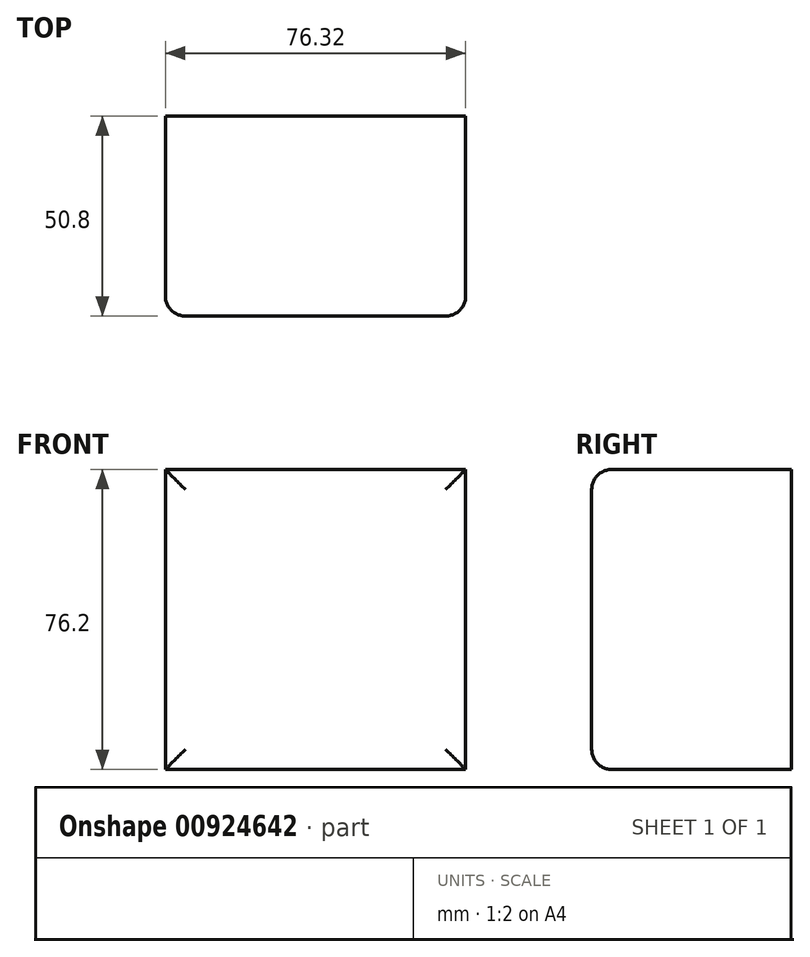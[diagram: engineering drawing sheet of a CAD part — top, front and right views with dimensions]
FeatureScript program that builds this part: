
annotation { "Feature Type Name" : "Feature", "Feature Type Description" : "" }
export const myFeature = defineFeature(function(context is Context, id is Id, definition is map)
    precondition{}
    {
        {
            var Q0;
            Q0=qCreatedBy(makeId("Front.planeOp"),FACE);
            var sketch = newSketch(context, id + "F0", { "sketchPlane" : qUnion([Q0])});
            skLineSegment(sketch, "E0", {"start": v(0, 0) * mm, "end": v(76.32, 0) * mm});
            skLineSegment(sketch, "E1", {"start": v(76.32, 0) * mm, "end": v(76.32, 76.2) * mm});
            skLineSegment(sketch, "E2", {"start": v(76.32, 76.2) * mm, "end": v(0, 76.2) * mm});
            skLineSegment(sketch, "E3", {"start": v(0, 76.2) * mm, "end": v(0, 0) * mm});
            skSolve(sketch);
        }
        {
            var Q0;
            Q0=makeQuery(id+"F0.imprint","IMPRINT",FACE,{"disambiguationData":[TD([[makeQuery(id+"F0.imprint","IMPRINT",EDGE,{"derivedFrom":sQuery(id+"F0.wireOp",EDGE,"E0")}),1.0]])]});
            extrude(context, id + "F1", {"entities" : qUnion([Q0]), "endBound" : BoundingType.SYMMETRIC, "depth" : 50.8 * mm, "offsetDistance" : 25.4 * mm, "hasSecondDirection" : true, "secondDirectionOppositeDirection" : true, "secondDirectionDepth" : 25.4 * mm});
        }
        {
            var Q0;
            Q0=makeQuery(id+"F1.opExtrude","CAP_EDGE",EDGE,{"disambiguationData":[OSD([sQuery(id+"F0.wireOp",EDGE,"E2")])],"isStart":false});
            var Q1;
            Q1=makeQuery(id+"F1.opExtrude","CAP_EDGE",EDGE,{"disambiguationData":[OSD([sQuery(id+"F0.wireOp",EDGE,"E1")])],"isStart":false});
            var Q2;
            Q2=makeQuery(id+"F1.opExtrude","CAP_EDGE",EDGE,{"disambiguationData":[OSD([sQuery(id+"F0.wireOp",EDGE,"E0")])],"isStart":false});
            var Q3;
            Q3=makeQuery(id+"F1.opExtrude","CAP_EDGE",EDGE,{"disambiguationData":[OSD([sQuery(id+"F0.wireOp",EDGE,"E3")])],"isStart":false});
            fillet(context, id + "F2", {"entities" : qUnion([Q0, Q1, Q2, Q3]), "radius" : 5.08 * mm, "tangentPropagation" : true, "allowEdgeOverflow" : false});
        }
    });
